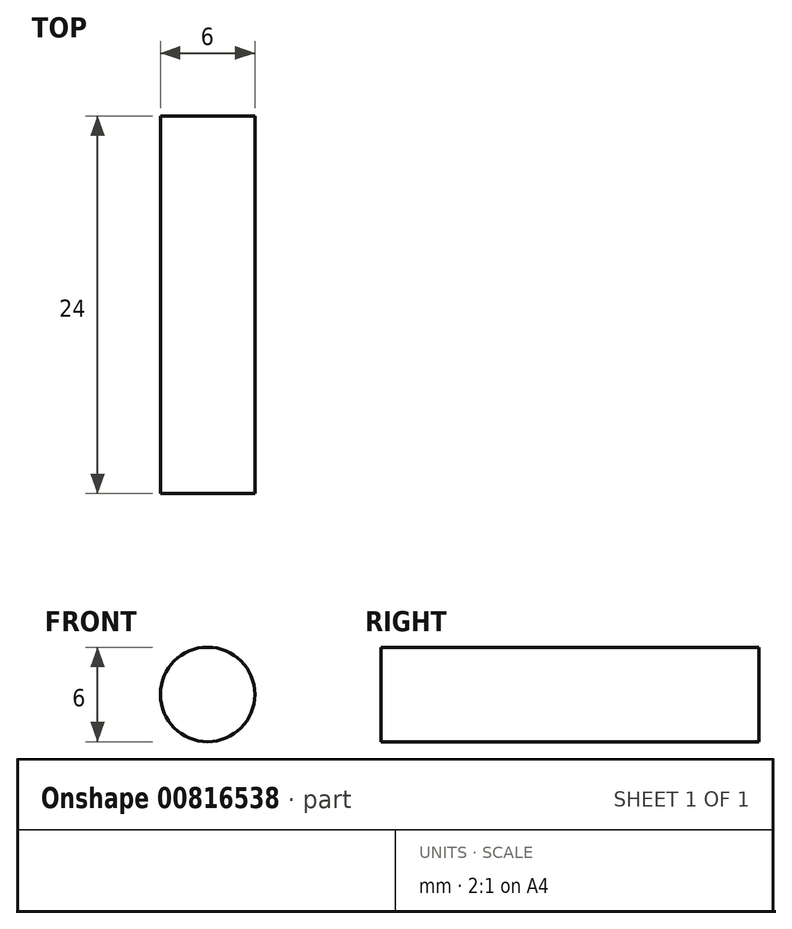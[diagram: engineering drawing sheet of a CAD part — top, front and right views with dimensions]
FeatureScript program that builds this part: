
annotation { "Feature Type Name" : "Feature", "Feature Type Description" : "" }
export const myFeature = defineFeature(function(context is Context, id is Id, definition is map)
    precondition{}
    {
        {
            assignVariable(context, id + "F0", {"name" : "Bolzenlaenge", "anyValue" : 24});
        }
        {
            var Q0;
            Q0=qCreatedBy(makeId("Front.planeOp"),FACE);
            var sketch = newSketch(context, id + "F1", { "sketchPlane" : qUnion([Q0])});
            skCircle(sketch, "E0", {"center": v(0, 0) * mm, "radius": 3 * mm});
            skSolve(sketch);
        }
        {
            var Q0;
            Q0=makeQuery(id+"F1.imprint","IMPRINT",FACE,{"disambiguationData":[TD([[makeQuery(id+"F1.imprint","IMPRINT",EDGE,{"derivedFrom":sQuery(id+"F1.wireOp",EDGE,"E0")}),1.0]])]});
            extrude(context, id + "F2", {"entities" : qUnion([Q0]), "depth" : (getVariable(context, 'Bolzenlaenge')) * mm, "offsetDistance" : 25 * mm});
        }
    });
